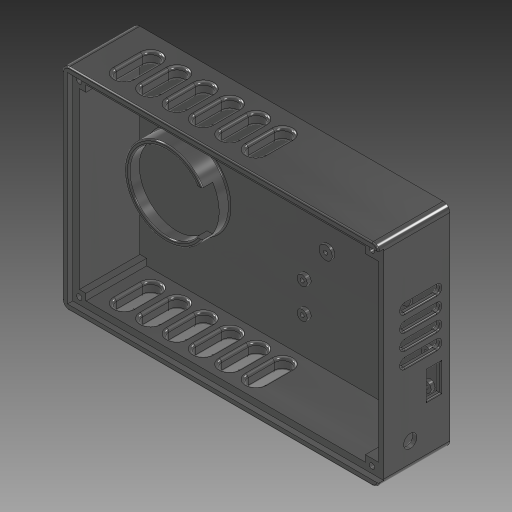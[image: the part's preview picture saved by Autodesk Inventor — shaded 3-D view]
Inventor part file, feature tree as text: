
AUTODESK INVENTOR PART (.ipt)
format: ipt  version: 2023 (Build 270158000, 158)  size: 1,212,928 bytes
history: native  units: mm
features: extrude x10, sketch x10, fillet x3, other x1, mirror x1
ambient origin geometry x8: Origin, YZ Plane, XZ Plane, XY Plane, X Axis, Y Axis, Z Axis, Center Point
bodies: Body1 (feature_tree)
feature tree (25):
  other  "Těleso1"
  extrude  "Vysunutí1"  Depth=120.0mm
  extrude  "Vysunutí2"  Depth=80.0mm
  extrude  "micro usb hole"  Depth=2.0mm TaperAngle=0.0deg
  extrude  "rpi holder"  Depth=116.0mm
  extrude  "rgb led hole"  Depth=25.0mm TaperAngle=0.0deg
  extrude  "ULN2003 holder"  Depth=3.5mm
  extrude  "Vysunutí10"  Depth=5.0mm
  extrude  "Vysunutí11"  Depth=10.0mm
  extrude  "Vysunutí12"  Depth=5.0mm TaperAngle=0.0deg
  extrude  "Vysunutí14"  Depth=3.8mm
  fillet  "Zaoblení1"  Radius=3.8mm
  fillet  "Zaoblení2"  Radius=11.4mm
  mirror  "Zrcadlit2"
  fillet  "Zaoblení3"  Radius=3.8mm
  sketch  "Náčrt1"
  sketch  "Náčrt2"
  sketch  "Náčrt3"
  sketch  "Náčrt4"
  sketch  "Náčrt6"
  sketch  "Náčrt7"
  sketch  "Náčrt10"
  sketch  "Náčrt11"
  sketch  "Náčrt12"
  sketch  "Náčrt15"
